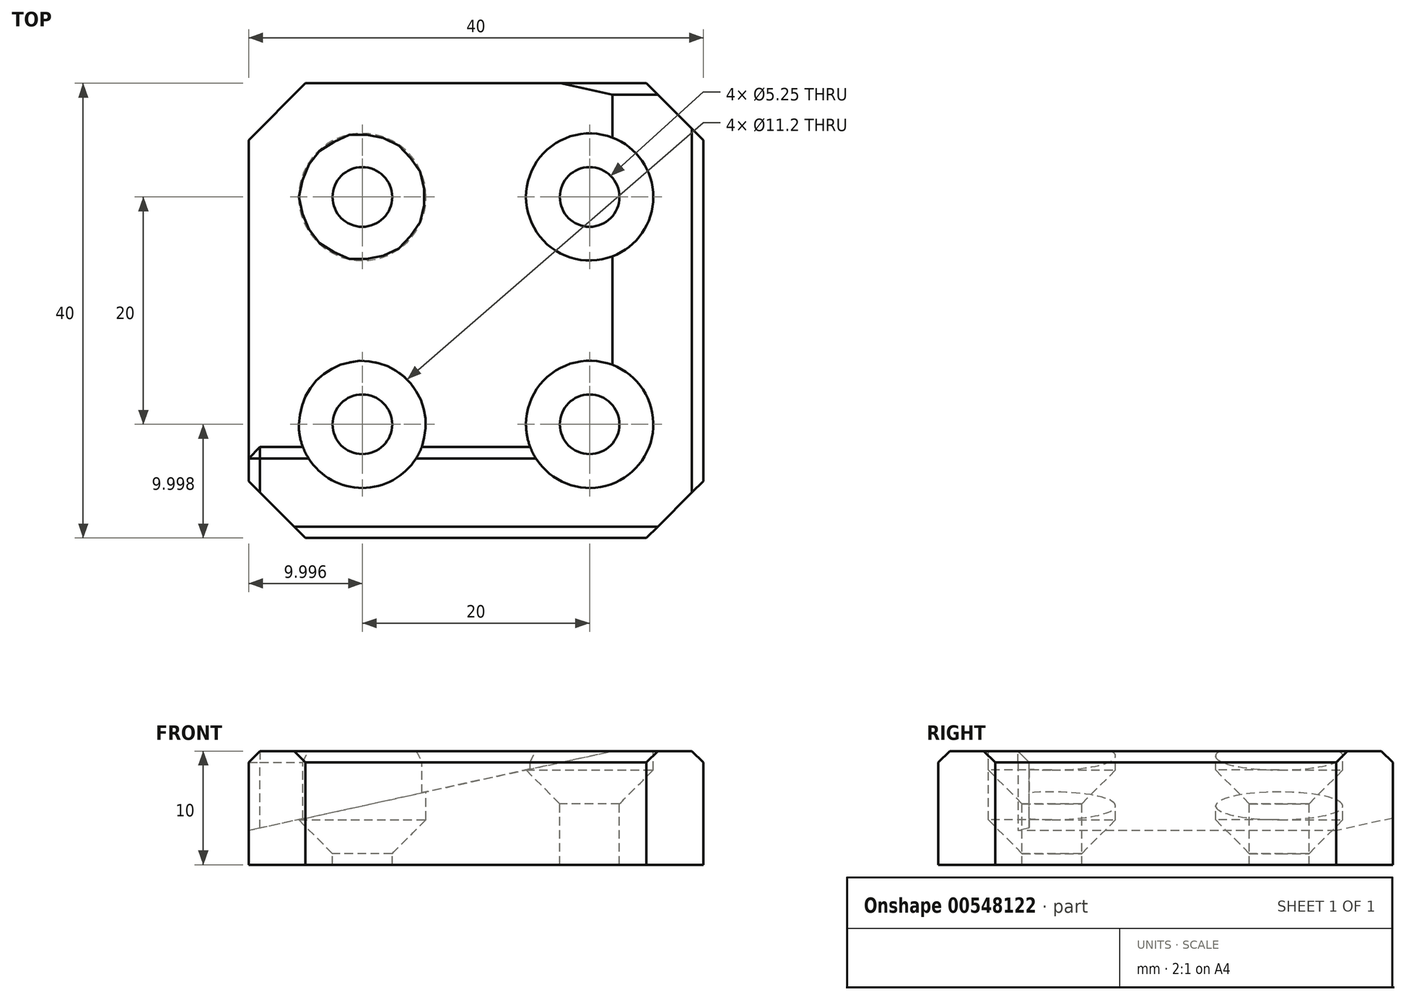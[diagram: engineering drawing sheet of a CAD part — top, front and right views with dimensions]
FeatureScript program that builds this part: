
annotation { "Feature Type Name" : "Feature", "Feature Type Description" : "" }
export const myFeature = defineFeature(function(context is Context, id is Id, definition is map)
    precondition{}
    {
        {
            var Q0;
            Q0=qCreatedBy(makeId("Top.planeOp"),FACE);
            var sketch = newSketch(context, id + "F0", { "sketchPlane" : qUnion([Q0])});
            skLineSegment(sketch, "E0.bottom", {"start": v(-28.36, 24.8) * mm, "end": v(11.64, 24.8) * mm});
            skLineSegment(sketch, "E0.top", {"start": v(-28.36, -15.2) * mm, "end": v(11.64, -15.2) * mm});
            skLineSegment(sketch, "E0.left", {"start": v(-28.36, 24.8) * mm, "end": v(-28.36, -15.2) * mm});
            skLineSegment(sketch, "E0.right", {"start": v(11.64, 24.8) * mm, "end": v(11.64, -15.2) * mm});
            skCircle(sketch, "E1", {"center": v(-18.36, 14.8) * mm, "radius": 5 * mm});
            skLineSegment(sketch, "E2", {"start": v(-8.36, 24.8) * mm, "end": v(-8.36, -15.2) * mm, "construction": true});
            skLineSegment(sketch, "E3", {"start": v(-28.36, 4.8) * mm, "end": v(11.64, 4.8) * mm, "construction": true});
            skCircle(sketch, "E4", {"center": v(-18.36, 14.8) * mm, "radius": 2.5 * mm});
            skCircle(sketch, "E5.MirrorC", {"center": v(1.64, 14.8) * mm, "radius": 5 * mm});
            skCircle(sketch, "E6.MirrorC", {"center": v(1.64, 14.8) * mm, "radius": 2.5 * mm});
            skCircle(sketch, "E7.MirrorC", {"center": v(1.64, -5.2) * mm, "radius": 5 * mm});
            skCircle(sketch, "E8.MirrorC", {"center": v(1.64, -5.2) * mm, "radius": 2.5 * mm});
            skCircle(sketch, "E9.MirrorC", {"center": v(-18.36, -5.2) * mm, "radius": 5 * mm});
            skCircle(sketch, "E10.MirrorC", {"center": v(-18.36, -5.2) * mm, "radius": 2.5 * mm});
            skSolve(sketch);
        }
        {
            var Q0;
            Q0=makeQuery(id+"F0.imprint","IMPRINT",FACE,{"disambiguationData":[TD([[makeQuery(id+"F0.imprint","IMPRINT",EDGE,{"derivedFrom":sQuery(id+"F0.wireOp",EDGE,"E0.bottom")}),-1.0]])]});
            var Q1;
            Q1=makeQuery(id+"F0.imprint","IMPRINT",FACE,{"disambiguationData":[TD([[makeQuery(id+"F0.imprint","IMPRINT",EDGE,{"derivedFrom":sQuery(id+"F0.wireOp",EDGE,"E1")}),1.0]])]});
            var Q2;
            Q2=makeQuery(id+"F0.imprint","IMPRINT",FACE,{"disambiguationData":[TD([[makeQuery(id+"F0.imprint","IMPRINT",EDGE,{"derivedFrom":sQuery(id+"F0.wireOp",EDGE,"E4")}),1.0]])]});
            var Q3;
            Q3=makeQuery(id+"F0.imprint","IMPRINT",FACE,{"disambiguationData":[TD([[makeQuery(id+"F0.imprint","IMPRINT",EDGE,{"derivedFrom":sQuery(id+"F0.wireOp",EDGE,"E5.MirrorC")}),-1.0]])]});
            var Q4;
            Q4=makeQuery(id+"F0.imprint","IMPRINT",FACE,{"disambiguationData":[TD([[makeQuery(id+"F0.imprint","IMPRINT",EDGE,{"derivedFrom":sQuery(id+"F0.wireOp",EDGE,"E6.MirrorC")}),-1.0]])]});
            var Q5;
            Q5=makeQuery(id+"F0.imprint","IMPRINT",FACE,{"disambiguationData":[TD([[makeQuery(id+"F0.imprint","IMPRINT",EDGE,{"derivedFrom":sQuery(id+"F0.wireOp",EDGE,"E7.MirrorC")}),1.0]])]});
            var Q6;
            Q6=makeQuery(id+"F0.imprint","IMPRINT",FACE,{"disambiguationData":[TD([[makeQuery(id+"F0.imprint","IMPRINT",EDGE,{"derivedFrom":sQuery(id+"F0.wireOp",EDGE,"E8.MirrorC")}),1.0]])]});
            var Q7;
            Q7=makeQuery(id+"F0.imprint","IMPRINT",FACE,{"disambiguationData":[TD([[makeQuery(id+"F0.imprint","IMPRINT",EDGE,{"derivedFrom":sQuery(id+"F0.wireOp",EDGE,"E9.MirrorC")}),-1.0]])]});
            var Q8;
            Q8=makeQuery(id+"F0.imprint","IMPRINT",FACE,{"disambiguationData":[TD([[makeQuery(id+"F0.imprint","IMPRINT",EDGE,{"derivedFrom":sQuery(id+"F0.wireOp",EDGE,"E10.MirrorC")}),-1.0]])]});
            extrude(context, id + "F1", {"entities" : qUnion([Q0, Q1, Q2, Q3, Q4, Q5, Q6, Q7, Q8]), "depth" : 10 * mm, "offsetDistance" : 25 * mm});
        }
        {
            var Q0;
            Q0=makeQuery(id+"F1.opExtrude","CAP_FACE",FACE,{"disambiguationData":[OSD([sQuery(id+"F0.wireOp",EDGE,"E0.bottom"),sQuery(id+"F0.wireOp",EDGE,"E0.top"),sQuery(id+"F0.wireOp",EDGE,"E0.left"),sQuery(id+"F0.wireOp",EDGE,"E0.right")])],"isStart":false});
            var sketch = newSketch(context, id + "F2", { "sketchPlane" : qUnion([Q0])});
            skLineSegment(sketch, "E11", {"start": v(-28.36, 14.8) * mm, "end": v(11.64, 14.8) * mm, "construction": true});
            skLineSegment(sketch, "E12", {"start": v(-28.36, -5.2) * mm, "end": v(11.64, -5.2) * mm, "construction": true});
            skLineSegment(sketch, "E13", {"start": v(-18.36, 24.8) * mm, "end": v(-18.36, -15.2) * mm, "construction": true});
            skLineSegment(sketch, "E14", {"start": v(1.64, 24.8) * mm, "end": v(1.64, -15.2) * mm});
            skPoint(sketch, "E15", {"position": v(-18.36, 14.8) * mm});
            skPoint(sketch, "E16", {"position": v(1.64, 14.8) * mm});
            skPoint(sketch, "E17", {"position": v(1.64, -5.2) * mm});
            skPoint(sketch, "E18", {"position": v(-18.36, -5.2) * mm});
            skSolve(sketch);
        }
        {
            var Q0;
            Q0=makeQuery(id+"F1.opExtrude","SWEPT_FACE",FACE,{"disambiguationData":[OSD([sQuery(id+"F0.wireOp",EDGE,"E0.top")])]});
            var sketch = newSketch(context, id + "F3", { "sketchPlane" : qUnion([Q0])});
            skLineSegment(sketch, "E19.bottom", {"start": v(-28.36, 0) * mm, "end": v(11.64, 0) * mm});
            skLineSegment(sketch, "E19.top", {"start": v(-28.36, 10) * mm, "end": v(11.64, 10) * mm});
            skLineSegment(sketch, "E19.left", {"start": v(-28.36, 0) * mm, "end": v(-28.36, 10) * mm});
            skLineSegment(sketch, "E19.right", {"start": v(11.64, 0) * mm, "end": v(11.64, 10) * mm});
            skSolve(sketch);
        }
        {
            var Q0;
            Q0=makeQuery(id+"F1.opExtrude","SWEPT_FACE",FACE,{"disambiguationData":[OSD([sQuery(id+"F0.wireOp",EDGE,"E0.top")])]});
            var sketch = newSketch(context, id + "F4", { "sketchPlane" : qUnion([Q0])});
            skLineSegment(sketch, "E20", {"start": v(-28.36, 3) * mm, "end": v(3.64, 10) * mm});
            skSolve(sketch);
        }
        {
            var Q0;
            {var subQ0=sQuery(id+"F4.wireOp",EDGE,"E20");Q0=makeQuery(id+"F4.imprint","IMPRINT",FACE,{"disambiguationData":[TD([[makeQuery(id+"F4.imprint","IMPRINT",EDGE,{"derivedFrom":subQ0}),1.0]])]});}
            var Q1;
            Q1=makeQuery(id+"F1.opExtrude","SWEPT_FACE",FACE,{"disambiguationData":[OSD([sQuery(id+"F0.wireOp",EDGE,"E0.bottom")])]});
            extrude(context, id + "F5", {"entities" : qUnion([Q0]), "operationType" : NewBodyOperationType.REMOVE, "endBound" : BoundingType.UP_TO_SURFACE, "oppositeDirection" : true, "depth" : 25 * mm, "endBoundEntityFace" : qUnion([Q1]), "offsetDistance" : 25 * mm});
        }
        {
            var Q0;
            {var subQ1=makeQuery(id+"F5.boolean.opBoolean","COPY",EDGE,{"derivedFrom":makeQuery(id+"F5.opExtrude","CAP_EDGE",EDGE,{"disambiguationData":[OSD([sQuery(id+"F4.wireOp",EDGE,"E20")])],"isStart":true})});Q0=makeQuery(id+"F3.imprint","IMPRINT",FACE,{"disambiguationData":[TD([[makeQuery(id+"F3.imprint","IMPRINT",EDGE,{"derivedFrom":subQ1}),1.0]])]});}
            var Q1;
            {var subQ1=sQuery(id+"F3.wireOp",EDGE,"E19.bottom");Q1=makeQuery(id+"F3.imprint","IMPRINT",FACE,{"disambiguationData":[TD([[makeQuery(id+"F3.imprint","IMPRINT",EDGE,{"derivedFrom":subQ1}),1.0]])]});}
            extrude(context, id + "F6", {"entities" : qUnion([Q0, Q1]), "operationType" : NewBodyOperationType.ADD, "oppositeDirection" : true, "depth" : 8 * mm, "offsetDistance" : 25 * mm});
        }
        {
            var Q0;
            Q0=sQuery(id+"F2.wireOp",VERTEX,"E15");
            var Q1;
            Q1=sQuery(id+"F2.wireOp",VERTEX,"E18");
            var Q2;
            Q2=sQuery(id+"F2.wireOp",VERTEX,"E17");
            var Q3;
            Q3=sQuery(id+"F2.wireOp",VERTEX,"E16");
            var Q4;
            Q4=makeQuery(id+"F1.opExtrude","SWEPT_BODY",BODY,{"disambiguationData":[OSD([sQuery(id+"F0.wireOp",EDGE,"E0.bottom"),sQuery(id+"F0.wireOp",EDGE,"E0.top"),sQuery(id+"F0.wireOp",EDGE,"E0.left"),sQuery(id+"F0.wireOp",EDGE,"E0.right")])]});
            hole(context, id + "F7", {"style" : HoleStyle.C_SINK, "endStyle" : HoleEndStyle.THROUGH, "standardTappedOrClearance" : lookupTablePath({ "standard" : "ISO", "fit" : "Close", "size" : "M5", "type" : "Clearance" }), "standardBlindInLast" : lookupTablePath({ "fit" : "Close", "standard" : "ISO", "size" : "M5", "type" : "Clearance" }), "holeDiameter" : 5.25 * mm, "cSinkDiameter" : 11.2 * mm, "cSinkAngle" : 90 * degree, "majorDiameter" : 5 * mm, "isTappedThrough" : true, "tappedDepth" : 12 * mm, "tapClearance" : 3, "locations" : qUnion([Q0, Q1, Q2, Q3]), "scope" : qUnion([Q4])});
        }
        {
            var Q0;
            Q0=makeQuery(id+"F6.opExtrude","CAP_EDGE",EDGE,{"disambiguationData":[OSD([sQuery(id+"F3.wireOp",EDGE,"E19.left")])],"isStart":false});
            var Q1;
            Q1=makeQuery(id+"F5.boolean.opBoolean","COPY",EDGE,{"derivedFrom":makeQuery(id+"F5.opExtrude","SWEPT_EDGE",EDGE,{"disambiguationData":[OSD([sQuery(id+"F0.wireOp",EDGE,"E0.top"),sQuery(id+"F0.wireOp",EDGE,"E0.left"),sQuery(id+"F4.wireOp",EDGE,"E20")])]})});
            var Q2;
            Q2=makeQuery(id+"F5.boolean.opBoolean","COPY",EDGE,{"derivedFrom":makeQuery(id+"F5.opExtrude","SWEPT_EDGE",EDGE,{"disambiguationData":[OSD([sQuery(id+"F0.wireOp",EDGE,"E0.top"),sQuery(id+"F4.wireOp",EDGE,"E20")])]})});
            var Q3;
            Q3=makeQuery(id+"F6.opExtrude","CAP_EDGE",EDGE,{"disambiguationData":[OSD([sQuery(id+"F3.wireOp",EDGE,"E19.top")])],"isStart":false});
            var Q4;
            Q4=makeQuery(id+"F6.boolean.opBoolean","MERGE",EDGE,{"derivedFrom":[makeQuery(id+"F1.opExtrude","CAP_EDGE",EDGE,{"disambiguationData":[OSD([sQuery(id+"F0.wireOp",EDGE,"E0.top")])],"isStart":false}),makeQuery(id+"F6.opExtrude","CAP_EDGE",EDGE,{"disambiguationData":[OSD([sQuery(id+"F3.wireOp",EDGE,"E19.top")])],"isStart":true})]});
            var Q5;
            Q5=makeQuery(id+"F1.opExtrude","CAP_EDGE",EDGE,{"disambiguationData":[OSD([sQuery(id+"F0.wireOp",EDGE,"E0.right")])],"isStart":false});
            var Q6;
            Q6=makeQuery(id+"F1.opExtrude","CAP_EDGE",EDGE,{"disambiguationData":[OSD([sQuery(id+"F0.wireOp",EDGE,"E0.bottom")])],"isStart":false});
            var Q7;
            Q7=makeQuery(id+"F5.boolean.opBoolean","COPY",EDGE,{"derivedFrom":makeQuery(id+"F5.opExtrude","TWEAK_EDGE",EDGE,{"derivedFrom":[makeQuery(id+"F1.opExtrude","SWEPT_FACE",FACE,{"disambiguationData":[OSD([sQuery(id+"F0.wireOp",EDGE,"E0.bottom")])]}),makeQuery(id+"F4.imprint","IMPRINT",EDGE,{"derivedFrom":sQuery(id+"F4.wireOp",EDGE,"E20")})]})});
            var Q8;
            Q8=makeQuery(id+"F6.opExtrude","SWEPT_EDGE",EDGE,{"disambiguationData":[OSD([sQuery(id+"F3.wireOp",EDGE,"E19.top"),sQuery(id+"F3.wireOp",EDGE,"E19.left")])]});
            chamfer(context, id + "F8", {"entities" : qUnion([Q0, Q1, Q2, Q3, Q4, Q5, Q6, Q7, Q8]), "width" : 1 * mm, "tangentPropagation" : true});
        }
        {
            var Q0;
            Q0=makeQuery(id+"F1.opExtrude","SWEPT_EDGE",EDGE,{"disambiguationData":[OSD([sQuery(id+"F0.wireOp",EDGE,"E0.bottom"),sQuery(id+"F0.wireOp",EDGE,"E0.right")])]});
            var Q1;
            Q1=makeQuery(id+"F1.opExtrude","SWEPT_EDGE",EDGE,{"disambiguationData":[OSD([sQuery(id+"F0.wireOp",EDGE,"E0.top"),sQuery(id+"F0.wireOp",EDGE,"E0.right")])]});
            var Q2;
            Q2=makeQuery(id+"F6.boolean.opBoolean","MERGE",EDGE,{"derivedFrom":[makeQuery(id+"F1.opExtrude","SWEPT_EDGE",EDGE,{"disambiguationData":[OSD([sQuery(id+"F0.wireOp",EDGE,"E0.top"),sQuery(id+"F0.wireOp",EDGE,"E0.left")])]}),makeQuery(id+"F6.opExtrude","CAP_EDGE",EDGE,{"disambiguationData":[OSD([sQuery(id+"F3.wireOp",EDGE,"E19.left")])],"isStart":true})]});
            var Q3;
            Q3=makeQuery(id+"F1.opExtrude","SWEPT_EDGE",EDGE,{"disambiguationData":[OSD([sQuery(id+"F0.wireOp",EDGE,"E0.bottom"),sQuery(id+"F0.wireOp",EDGE,"E0.left")])]});
            chamfer(context, id + "F9", {"entities" : qUnion([Q0, Q1, Q2, Q3]), "width" : 5 * mm, "tangentPropagation" : true});
        }
    });
